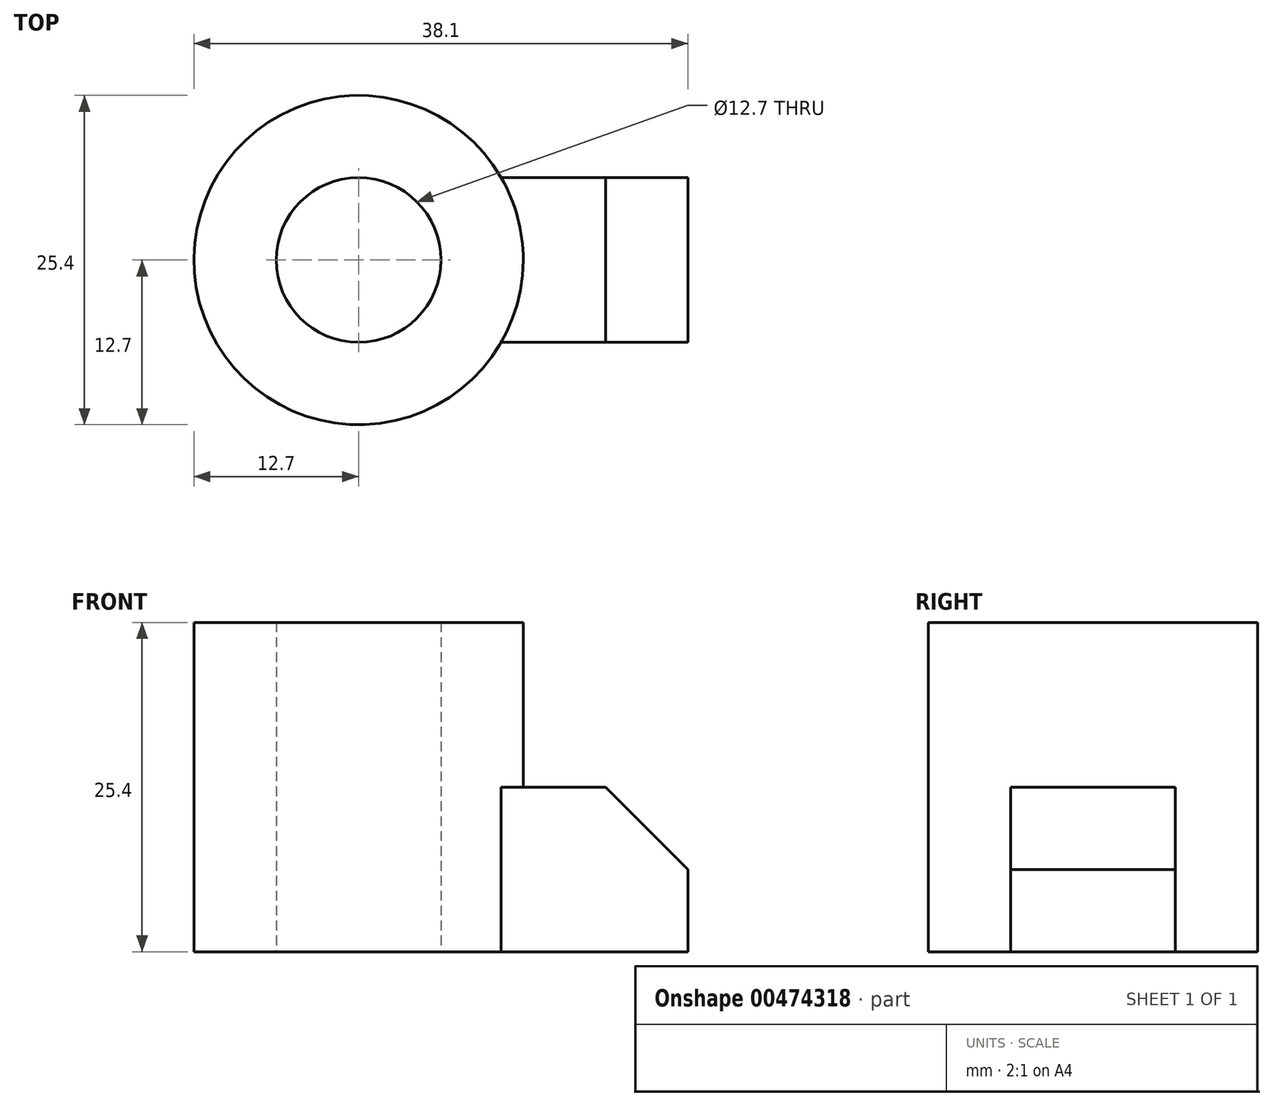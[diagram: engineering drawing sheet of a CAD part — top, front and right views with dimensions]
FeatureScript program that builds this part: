
annotation { "Feature Type Name" : "Feature", "Feature Type Description" : "" }
export const myFeature = defineFeature(function(context is Context, id is Id, definition is map)
    precondition{}
    {
        {
            var Q0;
            Q0=qCreatedBy(makeId("Top.planeOp"),FACE);
            var sketch = newSketch(context, id + "F0", { "sketchPlane" : qUnion([Q0])});
            skCircle(sketch, "E0", {"center": v(0, 0) * mm, "radius": 12.7 * mm});
            skCircle(sketch, "E1", {"center": v(0, 0) * mm, "radius": 6.35 * mm});
            skLineSegment(sketch, "E2", {"start": v(11, 6.35) * mm, "end": v(25.4, 6.35) * mm});
            skLineSegment(sketch, "E3", {"start": v(25.4, 6.35) * mm, "end": v(25.4, -6.35) * mm});
            skLineSegment(sketch, "E4", {"start": v(25.4, -6.35) * mm, "end": v(11, -6.35) * mm});
            skLineSegment(sketch, "E5", {"start": v(19.05, 6.35) * mm, "end": v(19.05, -6.35) * mm});
            skLineSegment(sketch, "E6", {"start": v(12.7, 0) * mm, "end": v(25.4, 0) * mm});
            skSolve(sketch);
        }
        {
            var Q0;
            Q0=makeQuery(id+"F0.imprint","IMPRINT",FACE,{"disambiguationData":[TD([[makeQuery(id+"F0.imprint","IMPRINT",EDGE,{"derivedFrom":sQuery(id+"F0.wireOp",EDGE,"E1")}),-1.0]])]});
            extrude(context, id + "F1", {"entities" : qUnion([Q0]), "depth" : 25.4 * mm});
        }
        {
            var Q0;
            {var subQ0=sQuery(id+"F0.wireOp",EDGE,"E4");var subQ1=sQuery(id+"F0.wireOp",EDGE,"E0");var subQ2=makeQuery(id+"F0.imprint","INTERSECT",VERTEX,{"derivedFrom":[subQ1,subQ0]});Q0=makeQuery(id+"F0.imprint","IMPRINT",FACE,{"disambiguationData":[TD([[makeQuery(id+"F0.imprint","IMPRINT",EDGE,{"disambiguationData":[TD([[subQ2,-1.0]])],"derivedFrom":subQ1}),-1.0]])]});}
            var Q1;
            {var subQ0=sQuery(id+"F0.wireOp",EDGE,"E2");var subQ1=sQuery(id+"F0.wireOp",EDGE,"E0");var subQ2=makeQuery(id+"F0.imprint","INTERSECT",VERTEX,{"derivedFrom":[subQ1,subQ0]});Q1=makeQuery(id+"F0.imprint","IMPRINT",FACE,{"disambiguationData":[TD([[makeQuery(id+"F0.imprint","IMPRINT",EDGE,{"disambiguationData":[TD([[subQ2,1.0]])],"derivedFrom":subQ1}),-1.0]])]});}
            var Q2;
            {var subQ0=sQuery(id+"F0.wireOp",EDGE,"E3");var subQ1=sQuery(id+"F0.wireOp",EDGE,"E2");var subQ2=makeQuery(id+"F0.imprint","INTERSECT",VERTEX,{"derivedFrom":[subQ1,subQ0]});Q2=makeQuery(id+"F0.imprint","IMPRINT",FACE,{"disambiguationData":[TD([[makeQuery(id+"F0.imprint","IMPRINT",EDGE,{"disambiguationData":[TD([[subQ2,1.0]])],"derivedFrom":subQ1}),-1.0]])]});}
            var Q3;
            {var subQ0=sQuery(id+"F0.wireOp",EDGE,"E4");var subQ1=sQuery(id+"F0.wireOp",EDGE,"E3");var subQ2=makeQuery(id+"F0.imprint","INTERSECT",VERTEX,{"derivedFrom":[subQ1,subQ0]});Q3=makeQuery(id+"F0.imprint","IMPRINT",FACE,{"disambiguationData":[TD([[makeQuery(id+"F0.imprint","IMPRINT",EDGE,{"disambiguationData":[TD([[subQ2,1.0]])],"derivedFrom":subQ1}),-1.0]])]});}
            extrude(context, id + "F2", {"entities" : qUnion([Q0, Q1, Q2, Q3]), "operationType" : NewBodyOperationType.ADD, "depth" : 12.7 * mm});
        }
        {
            var Q0;
            Q0=makeQuery(id+"F2.opExtrude","CAP_EDGE",EDGE,{"disambiguationData":[OSD([sQuery(id+"F0.wireOp",EDGE,"E3")])],"isStart":false});
            chamfer(context, id + "F3", {"entities" : qUnion([Q0]), "width" : 6.35 * mm, "tangentPropagation" : true});
        }
    });
